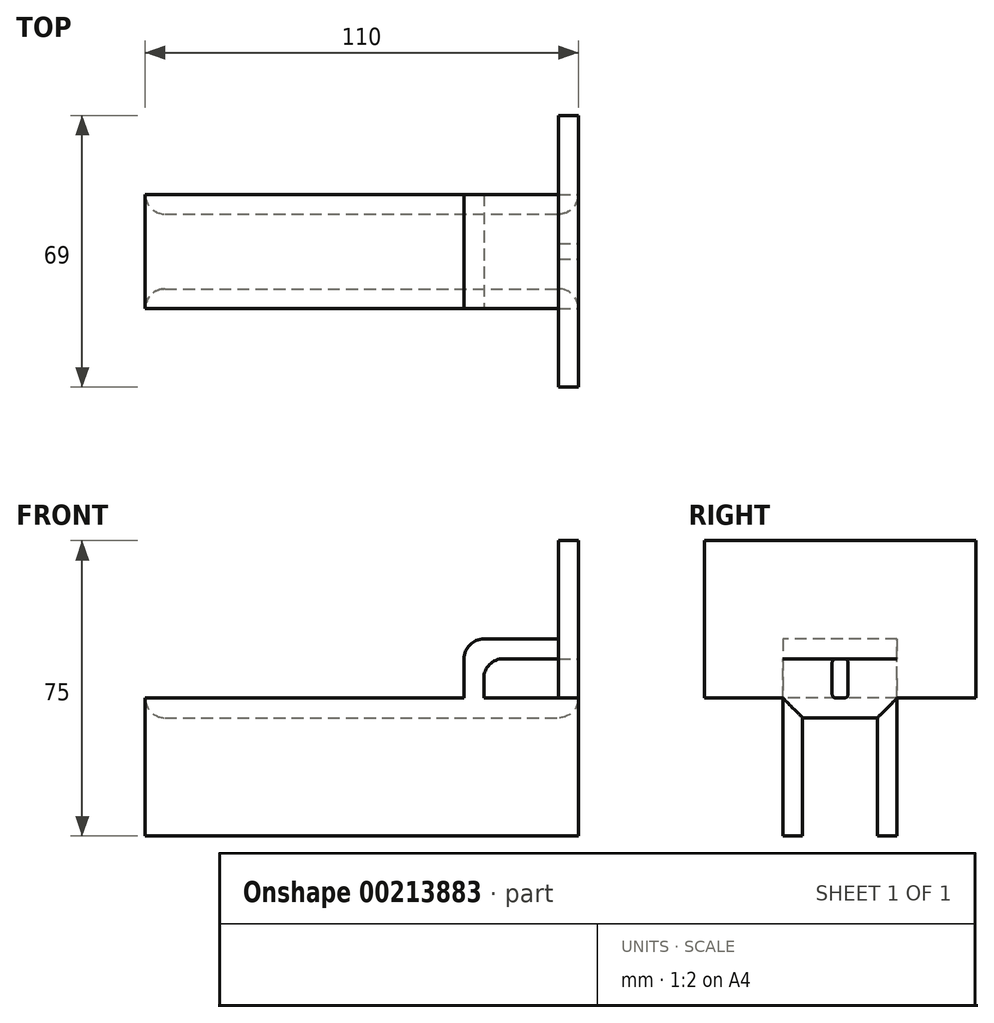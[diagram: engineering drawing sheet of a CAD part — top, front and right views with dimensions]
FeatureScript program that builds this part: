
annotation { "Feature Type Name" : "Feature", "Feature Type Description" : "" }
export const myFeature = defineFeature(function(context is Context, id is Id, definition is map)
    precondition{}
    {
        {
            var Q0;
            Q0=qCreatedBy(makeId("Right.planeOp"),FACE);
            var sketch = newSketch(context, id + "F0", { "sketchPlane" : qUnion([Q0])});
            skLineSegment(sketch, "E0", {"start": v(0, -30) * mm, "end": v(0, 0) * mm});
            skLineSegment(sketch, "E1", {"start": v(0, 0) * mm, "end": v(19, 0) * mm});
            skLineSegment(sketch, "E2", {"start": v(19, 0) * mm, "end": v(19, -30) * mm});
            skLineSegment(sketch, "E3", {"start": v(19, -30) * mm, "end": v(24, -30) * mm});
            skLineSegment(sketch, "E4", {"start": v(24, -30) * mm, "end": v(24, 5) * mm});
            skLineSegment(sketch, "E5", {"start": v(24, 5) * mm, "end": v(-5, 5) * mm});
            skLineSegment(sketch, "E6", {"start": v(-5, 5) * mm, "end": v(-5, -30) * mm});
            skLineSegment(sketch, "E7", {"start": v(-5, -30) * mm, "end": v(0, -30) * mm});
            skSolve(sketch);
        }
        {
            var Q0;
            Q0=makeQuery(id+"F0.imprint","IMPRINT",FACE,{"disambiguationData":[TD([[makeQuery(id+"F0.imprint","IMPRINT",EDGE,{"derivedFrom":sQuery(id+"F0.wireOp",EDGE,"E0")}),1.0]])]});
            extrude(context, id + "F1", {"entities" : qUnion([Q0]), "oppositeDirection" : true, "depth" : 110 * mm, "offsetDistance" : 25 * mm});
        }
        {
            var Q0;
            Q0=makeQuery(id+"F1.opExtrude","CAP_FACE",FACE,{"disambiguationData":[OSD([sQuery(id+"F0.wireOp",EDGE,"E0"),sQuery(id+"F0.wireOp",EDGE,"E1"),sQuery(id+"F0.wireOp",EDGE,"E2"),sQuery(id+"F0.wireOp",EDGE,"E3"),sQuery(id+"F0.wireOp",EDGE,"E4"),sQuery(id+"F0.wireOp",EDGE,"E5"),sQuery(id+"F0.wireOp",EDGE,"E6"),sQuery(id+"F0.wireOp",EDGE,"E7")])],"isStart":true});
            var sketch = newSketch(context, id + "F2", { "sketchPlane" : qUnion([Q0])});
            skLineSegment(sketch, "E8", {"start": v(-5, 5) * mm, "end": v(-25, 5) * mm});
            skLineSegment(sketch, "E9", {"start": v(-25, 5) * mm, "end": v(-25, 45) * mm});
            skLineSegment(sketch, "E10", {"start": v(-25, 45) * mm, "end": v(44, 45) * mm});
            skLineSegment(sketch, "E11", {"start": v(44, 45) * mm, "end": v(44, 5) * mm});
            skLineSegment(sketch, "E12", {"start": v(44, 5) * mm, "end": v(-5, 5) * mm});
            skSolve(sketch);
        }
        {
            var Q0;
            {var subQ1=sQuery(id+"F2.wireOp",EDGE,"E8");Q0=makeQuery(id+"F2.imprint","IMPRINT",FACE,{"disambiguationData":[TD([[makeQuery(id+"F2.imprint","IMPRINT",EDGE,{"derivedFrom":subQ1}),-1.0]])]});}
            extrude(context, id + "F3", {"entities" : qUnion([Q0]), "operationType" : NewBodyOperationType.ADD, "oppositeDirection" : true, "depth" : 5 * mm, "offsetDistance" : 25 * mm});
        }
        {
            var Q0;
            Q0=makeQuery(id+"F1.opExtrude","SWEPT_FACE",FACE,{"disambiguationData":[OSD([sQuery(id+"F0.wireOp",EDGE,"E6")])]});
            var sketch = newSketch(context, id + "F4", { "sketchPlane" : qUnion([Q0])});
            skLineSegment(sketch, "E13", {"start": v(-5, 15) * mm, "end": v(-19, 15) * mm});
            skLineSegment(sketch, "E14", {"start": v(-24, 10) * mm, "end": v(-24, 5) * mm});
            skLineSegment(sketch, "E15", {"start": v(-24, 5) * mm, "end": v(-29, 5) * mm});
            skLineSegment(sketch, "E16", {"start": v(-29, 5) * mm, "end": v(-29, 15) * mm});
            skLineSegment(sketch, "E17", {"start": v(-24, 20) * mm, "end": v(-5, 20) * mm});
            skLineSegment(sketch, "E18", {"start": v(-5, 20) * mm, "end": v(-5, 15) * mm});
            skLineSegment(sketch, "E19", {"start": v(-5, 15) * mm, "end": v(-5, 20) * mm});
            skPoint(sketch, "E20.visualSharp", {"position": v(-24, 15) * mm});
            skArc(sketch, "E20.filletArc", {"start": v(-19, 15) * mm, "mid": v(-22.54, 13.54) * mm, "end": v(-24, 10) * mm});
            skPoint(sketch, "E21.visualSharp", {"position": v(-29, 20) * mm});
            skArc(sketch, "E21.filletArc", {"start": v(-24, 20) * mm, "mid": v(-27.54, 18.54) * mm, "end": v(-29, 15) * mm});
            skSolve(sketch);
        }
        {
            var Q0;
            Q0=makeQuery(id+"F4.imprint","IMPRINT",FACE,{"disambiguationData":[TD([[makeQuery(id+"F4.imprint","IMPRINT",EDGE,{"derivedFrom":sQuery(id+"F4.wireOp",EDGE,"E13")}),-1.0]])]});
            var Q1;
            Q1=makeQuery(id+"F1.opExtrude","SWEPT_FACE",FACE,{"disambiguationData":[OSD([sQuery(id+"F0.wireOp",EDGE,"E4")])]});
            extrude(context, id + "F5", {"entities" : qUnion([Q0]), "operationType" : NewBodyOperationType.ADD, "endBound" : BoundingType.UP_TO_SURFACE, "oppositeDirection" : true, "depth" : 25 * mm, "endBoundEntityFace" : qUnion([Q1]), "offsetDistance" : 25 * mm});
        }
        {
            var Q0;
            Q0=makeQuery(id+"F3.boolean.opBoolean","MERGE",FACE,{"derivedFrom":[makeQuery(id+"F1.opExtrude","CAP_FACE",FACE,{"disambiguationData":[OSD([sQuery(id+"F0.wireOp",EDGE,"E0"),sQuery(id+"F0.wireOp",EDGE,"E1"),sQuery(id+"F0.wireOp",EDGE,"E2"),sQuery(id+"F0.wireOp",EDGE,"E3"),sQuery(id+"F0.wireOp",EDGE,"E4"),sQuery(id+"F0.wireOp",EDGE,"E5"),sQuery(id+"F0.wireOp",EDGE,"E6"),sQuery(id+"F0.wireOp",EDGE,"E7")])],"isStart":true}),makeQuery(id+"F3.opExtrude","CAP_FACE",FACE,{"disambiguationData":[OSD([sQuery(id+"F2.wireOp",EDGE,"E8"),sQuery(id+"F2.wireOp",EDGE,"E9"),sQuery(id+"F2.wireOp",EDGE,"E10"),sQuery(id+"F2.wireOp",EDGE,"E11"),sQuery(id+"F2.wireOp",EDGE,"E12")])],"isStart":true})]});
            var sketch = newSketch(context, id + "F6", { "sketchPlane" : qUnion([Q0])});
            skLineSegment(sketch, "E22", {"start": v(9.5, 5) * mm, "end": v(10.5, 5) * mm});
            skPoint(sketch, "E22.startSnap0", {"position": v(9.5, 0) * mm});
            skLineSegment(sketch, "E23", {"start": v(11.5, 6) * mm, "end": v(11.5, 14) * mm});
            skLineSegment(sketch, "E24", {"start": v(10.5, 15) * mm, "end": v(8.5, 15) * mm});
            skLineSegment(sketch, "E25", {"start": v(7.5, 14) * mm, "end": v(7.5, 6) * mm});
            skLineSegment(sketch, "E26", {"start": v(8.5, 5) * mm, "end": v(9.5, 5) * mm});
            skPoint(sketch, "E27.visualSharp", {"position": v(7.5, 15) * mm});
            skArc(sketch, "E27.filletArc", {"start": v(8.5, 15) * mm, "mid": v(7.8, 14.7) * mm, "end": v(7.5, 14) * mm});
            skPoint(sketch, "E28.visualSharp", {"position": v(11.5, 15) * mm});
            skArc(sketch, "E28.filletArc", {"start": v(11.5, 14) * mm, "mid": v(11.2, 14.7) * mm, "end": v(10.5, 15) * mm});
            skPoint(sketch, "E29.visualSharp", {"position": v(11.5, 5) * mm});
            skArc(sketch, "E29.filletArc", {"start": v(10.5, 5) * mm, "mid": v(11.2, 5.3) * mm, "end": v(11.5, 6) * mm});
            skPoint(sketch, "E30.visualSharp", {"position": v(7.5, 5) * mm});
            skArc(sketch, "E30.filletArc", {"start": v(7.5, 6) * mm, "mid": v(7.8, 5.3) * mm, "end": v(8.5, 5) * mm});
            skSolve(sketch);
        }
        {
            var Q0;
            Q0=makeQuery(id+"F6.imprint","IMPRINT",FACE,{"disambiguationData":[TD([[makeQuery(id+"F6.imprint","IMPRINT",EDGE,{"derivedFrom":sQuery(id+"F6.wireOp",EDGE,"E22")}),1.0]])]});
            extrude(context, id + "F7", {"entities" : qUnion([Q0]), "operationType" : NewBodyOperationType.REMOVE, "endBound" : BoundingType.UP_TO_NEXT, "oppositeDirection" : true, "depth" : 40 * mm, "offsetDistance" : 25 * mm});
        }
        {
            var Q0;
            Q0=makeQuery(id+"F1.opExtrude","CAP_EDGE",EDGE,{"disambiguationData":[OSD([sQuery(id+"F0.wireOp",EDGE,"E2")])],"isStart":false});
            var Q1;
            Q1=makeQuery(id+"F1.opExtrude","CAP_EDGE",EDGE,{"disambiguationData":[OSD([sQuery(id+"F0.wireOp",EDGE,"E1")])],"isStart":false});
            var Q2;
            Q2=makeQuery(id+"F1.opExtrude","CAP_EDGE",EDGE,{"disambiguationData":[OSD([sQuery(id+"F0.wireOp",EDGE,"E0")])],"isStart":false});
            fillet(context, id + "F8", {"entities" : qUnion([Q0, Q1, Q2]), "tangentPropagation" : true, "radius" : 5 * mm, "defaultsChanged" : false, "vertexSettings" : [], "allowEdgeOverflow" : false});
        }
        {
            var Q0;
            Q0=makeQuery(id+"F1.opExtrude","CAP_EDGE",EDGE,{"disambiguationData":[OSD([sQuery(id+"F0.wireOp",EDGE,"E0")])],"isStart":true});
            var Q1;
            Q1=makeQuery(id+"F1.opExtrude","CAP_EDGE",EDGE,{"disambiguationData":[OSD([sQuery(id+"F0.wireOp",EDGE,"E2")])],"isStart":true});
            var Q2;
            Q2=makeQuery(id+"F1.opExtrude","CAP_EDGE",EDGE,{"disambiguationData":[OSD([sQuery(id+"F0.wireOp",EDGE,"E1")])],"isStart":true});
            fillet(context, id + "F9", {"entities" : qUnion([Q0, Q1, Q2]), "tangentPropagation" : true, "radius" : 5 * mm, "defaultsChanged" : false, "vertexSettings" : [], "allowEdgeOverflow" : false});
        }
    });
